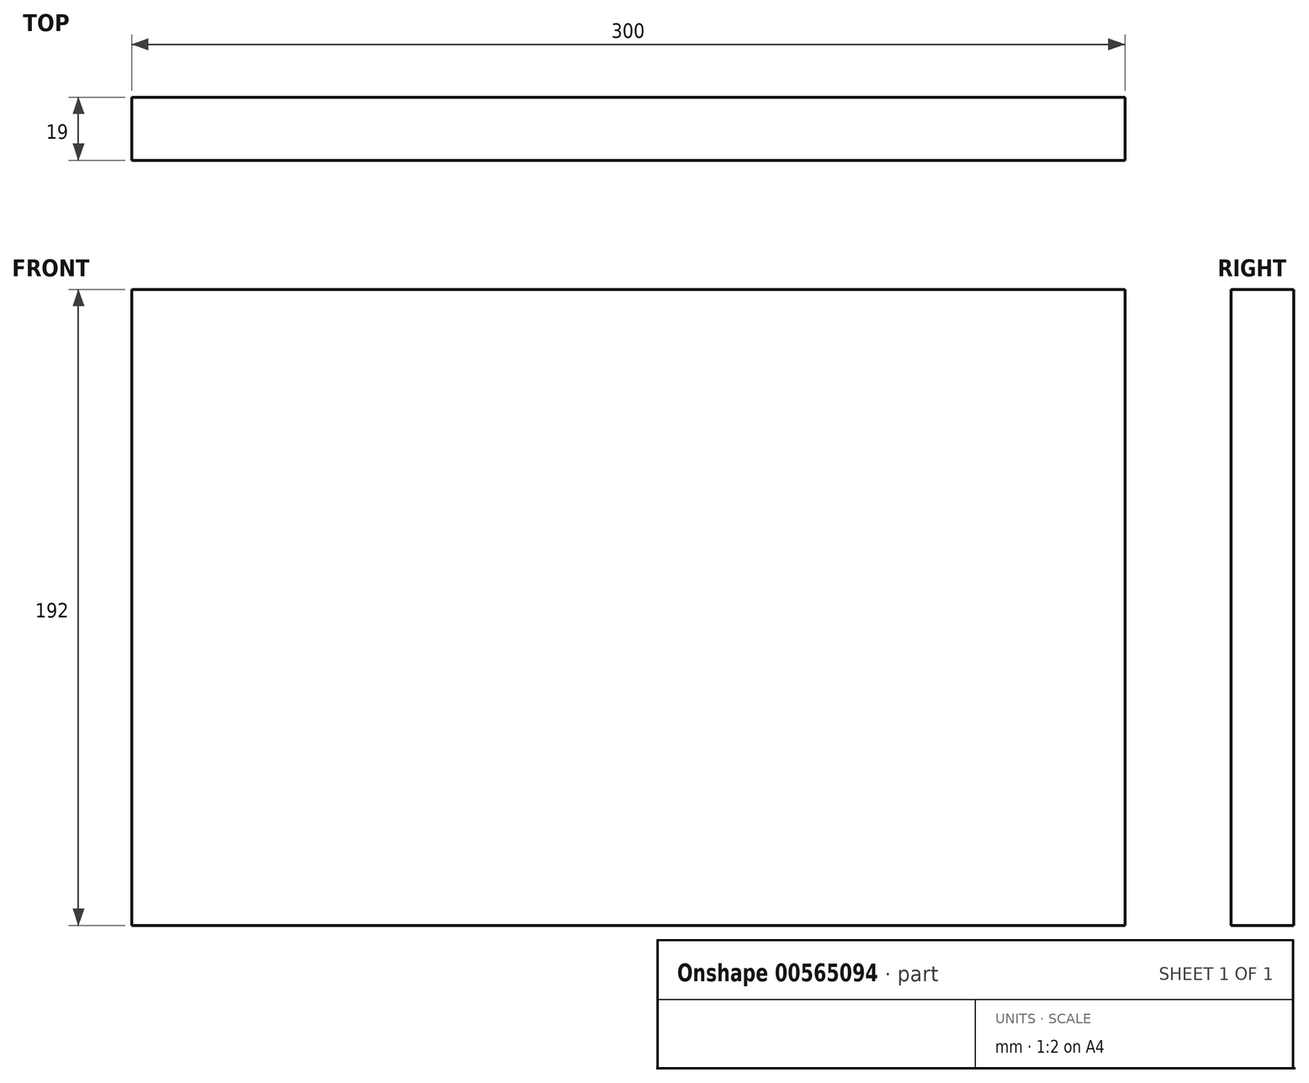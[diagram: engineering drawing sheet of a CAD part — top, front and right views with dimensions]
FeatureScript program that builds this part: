
annotation { "Feature Type Name" : "Feature", "Feature Type Description" : "" }
export const myFeature = defineFeature(function(context is Context, id is Id, definition is map)
    precondition{}
    {
        {
            var Q0;
            Q0=qCreatedBy(makeId("Front.planeOp"),FACE);
            var sketch = newSketch(context, id + "F0", { "sketchPlane" : qUnion([Q0])});
            skLineSegment(sketch, "E0.bottom", {"start": v(-139.59, 95.04) * mm, "end": v(160.41, 95.04) * mm});
            skLineSegment(sketch, "E0.top", {"start": v(-139.59, -96.96) * mm, "end": v(160.41, -96.96) * mm});
            skLineSegment(sketch, "E0.left", {"start": v(-139.59, 95.04) * mm, "end": v(-139.59, -96.96) * mm});
            skLineSegment(sketch, "E0.right", {"start": v(160.41, 95.04) * mm, "end": v(160.41, -96.96) * mm});
            skSolve(sketch);
        }
        {
            var Q0;
            Q0=makeQuery(id+"F0.imprint","IMPRINT",FACE,{"disambiguationData":[TD([[makeQuery(id+"F0.imprint","IMPRINT",EDGE,{"derivedFrom":sQuery(id+"F0.wireOp",EDGE,"E0.bottom")}),-1.0]])]});
            extrude(context, id + "F1", {"entities" : qUnion([Q0]), "depth" : 19 * mm, "offsetDistance" : 25 * mm});
        }
    });
